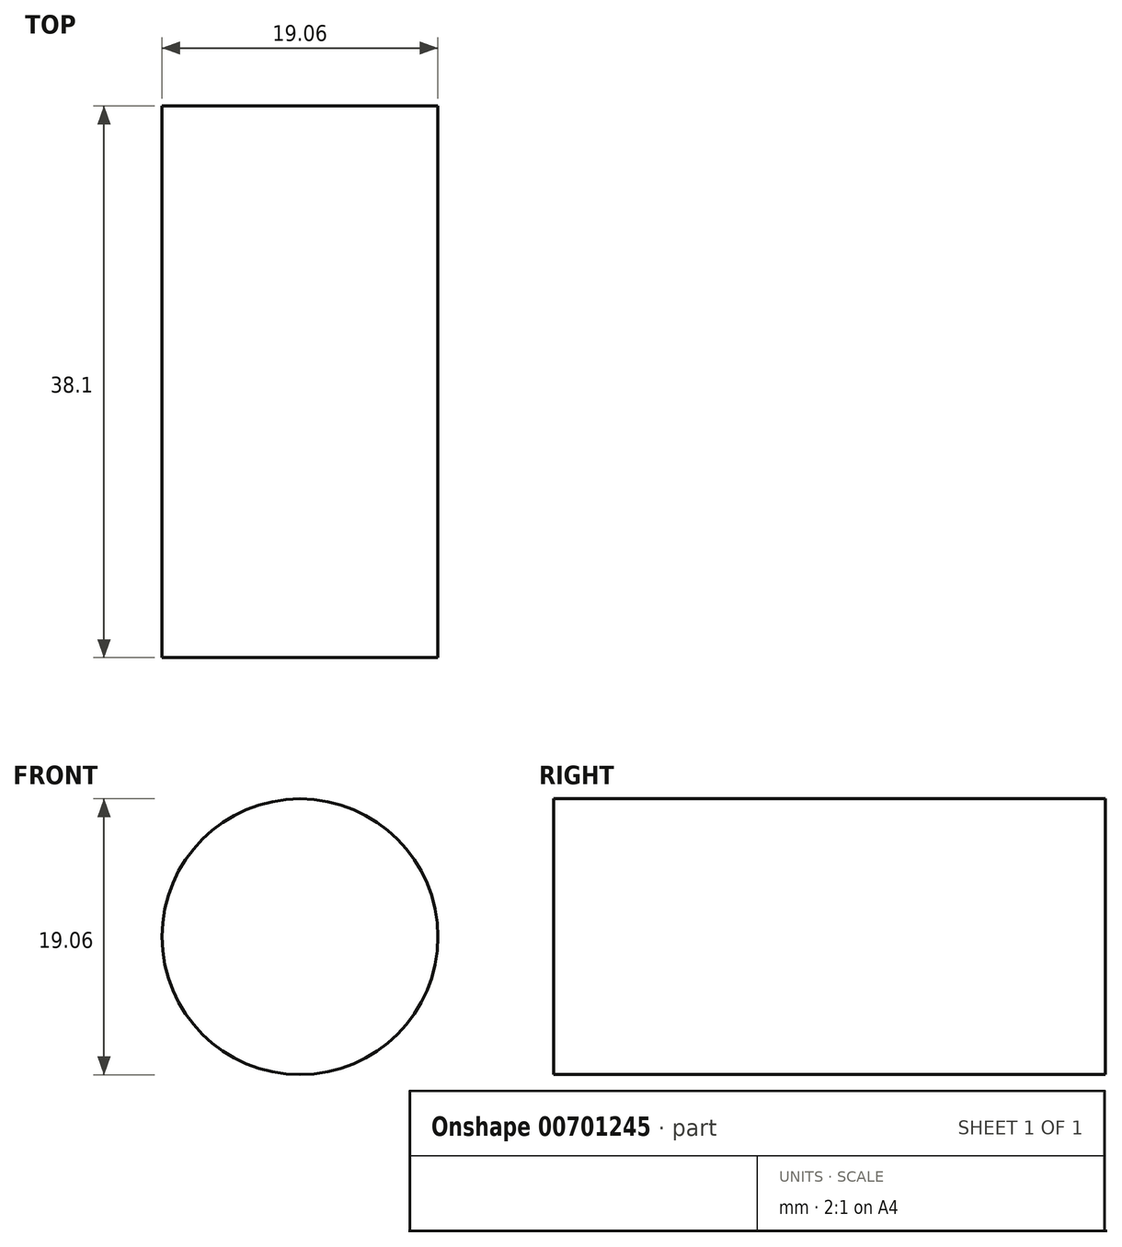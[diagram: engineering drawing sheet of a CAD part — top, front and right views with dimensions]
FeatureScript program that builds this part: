
annotation { "Feature Type Name" : "Feature", "Feature Type Description" : "" }
export const myFeature = defineFeature(function(context is Context, id is Id, definition is map)
    precondition{}
    {
        {
            var Q0;
            Q0=qCreatedBy(makeId("Front.planeOp"),FACE);
            var sketch = newSketch(context, id + "F0", { "sketchPlane" : qUnion([Q0])});
            skCircle(sketch, "E0", {"center": v(0, 0) * mm, "radius": 9.53 * mm});
            skSolve(sketch);
        }
        {
            var Q0;
            Q0=makeQuery(id+"F0.imprint","IMPRINT",FACE,{"disambiguationData":[TD([[makeQuery(id+"F0.imprint","IMPRINT",EDGE,{"derivedFrom":sQuery(id+"F0.wireOp",EDGE,"E0")}),1.0]])]});
            extrude(context, id + "F1", {"entities" : qUnion([Q0]), "depth" : 38.1 * mm, "offsetDistance" : 25.4 * mm});
        }
    });
